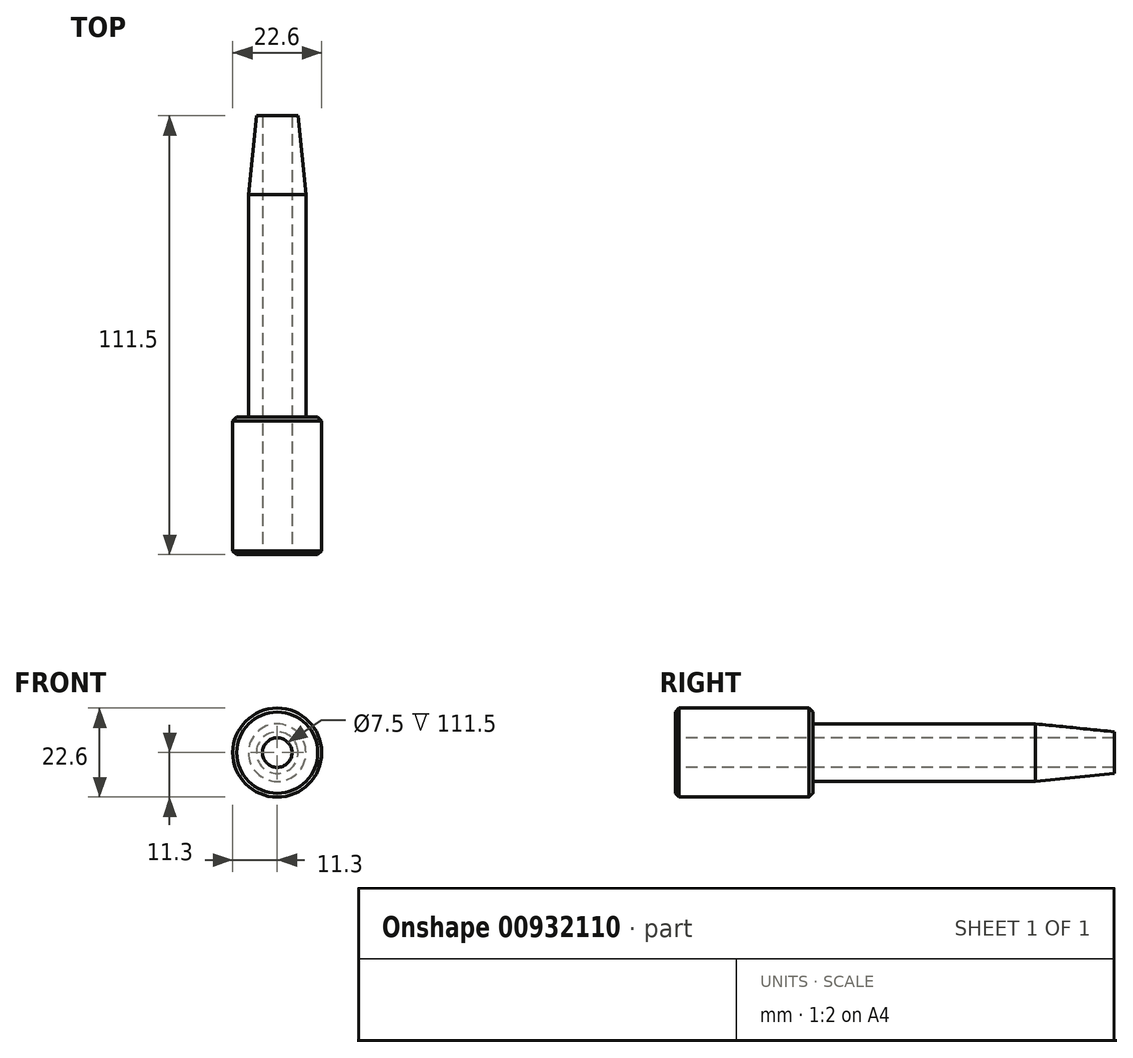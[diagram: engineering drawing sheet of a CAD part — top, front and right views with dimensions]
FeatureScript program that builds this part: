
annotation { "Feature Type Name" : "Feature", "Feature Type Description" : "" }
export const myFeature = defineFeature(function(context is Context, id is Id, definition is map)
    precondition{}
    {
        {
            var Q0;
            Q0=qCreatedBy(makeId("Front.planeOp"),FACE);
            var sketch = newSketch(context, id + "F0", { "sketchPlane" : qUnion([Q0])});
            skCircle(sketch, "E0", {"center": v(0, 0) * mm, "radius": 11.3 * mm});
            skSolve(sketch);
        }
        {
            var Q0;
            Q0=makeQuery(id+"F0.imprint","IMPRINT",FACE,{"disambiguationData":[TD([[makeQuery(id+"F0.imprint","IMPRINT",EDGE,{"derivedFrom":sQuery(id+"F0.wireOp",EDGE,"E0")}),1.0]])]});
            extrude(context, id + "F1", {"entities" : qUnion([Q0]), "oppositeDirection" : true, "depth" : 35 * mm, "offsetDistance" : 25 * mm});
        }
        {
            var Q0;
            Q0=makeQuery(id+"F1.opExtrude","CAP_EDGE",EDGE,{"disambiguationData":[OSD([sQuery(id+"F0.wireOp",EDGE,"E0")])],"isStart":true});
            chamfer(context, id + "F2", {"entities" : qUnion([Q0]), "width" : 1 * mm, "tangentPropagation" : true});
        }
        {
            var Q0;
            Q0=makeQuery(id+"F1.opExtrude","CAP_FACE",FACE,{"disambiguationData":[OSD([sQuery(id+"F0.wireOp",EDGE,"E0")])],"isStart":false});
            var sketch = newSketch(context, id + "F3", { "sketchPlane" : qUnion([Q0])});
            skCircle(sketch, "E1", {"center": v(0, 0) * mm, "radius": 7.3 * mm});
            skSolve(sketch);
        }
        {
            var Q0;
            Q0=makeQuery(id+"F3.imprint","IMPRINT",FACE,{"disambiguationData":[TD([[makeQuery(id+"F3.imprint","IMPRINT",EDGE,{"derivedFrom":sQuery(id+"F3.wireOp",EDGE,"E1")}),1.0]])]});
            extrude(context, id + "F4", {"entities" : qUnion([Q0]), "operationType" : NewBodyOperationType.ADD, "depth" : 76.5 * mm, "offsetDistance" : 25 * mm});
        }
        {
            var Q0;
            Q0=makeQuery(id+"F4.opExtrude","CAP_EDGE",EDGE,{"disambiguationData":[OSD([sQuery(id+"F3.wireOp",EDGE,"E1")])],"isStart":false});
            chamfer(context, id + "F5", {"entities" : qUnion([Q0]), "chamferType" : ChamferType.TWO_OFFSETS, "width1" : 2 * mm, "oppositeDirection" : false, "width2" : 20 * mm, "tangentPropagation" : true});
        }
        {
            var Q0;
            Q0=makeQuery(id+"F1.opExtrude","CAP_FACE",FACE,{"disambiguationData":[OSD([sQuery(id+"F0.wireOp",EDGE,"E0")])],"isStart":true});
            var sketch = newSketch(context, id + "F6", { "sketchPlane" : qUnion([Q0])});
            skCircle(sketch, "E2", {"center": v(0, 0) * mm, "radius": 3.75 * mm});
            skSolve(sketch);
        }
        {
            var Q0;
            Q0=makeQuery(id+"F6.imprint","IMPRINT",FACE,{"disambiguationData":[TD([[makeQuery(id+"F6.imprint","IMPRINT",EDGE,{"derivedFrom":sQuery(id+"F6.wireOp",EDGE,"E2")}),1.0]])]});
            extrude(context, id + "F7", {"entities" : qUnion([Q0]), "operationType" : NewBodyOperationType.REMOVE, "endBound" : BoundingType.THROUGH_ALL, "oppositeDirection" : true, "depth" : 25 * mm, "offsetDistance" : 25 * mm});
        }
        {
            var Q0;
            Q0=makeQuery(id+"F1.opExtrude","CAP_EDGE",EDGE,{"disambiguationData":[OSD([sQuery(id+"F0.wireOp",EDGE,"E0")])],"isStart":false});
            chamfer(context, id + "F8", {"entities" : qUnion([Q0]), "width" : 1 * mm, "tangentPropagation" : true});
        }
    });
